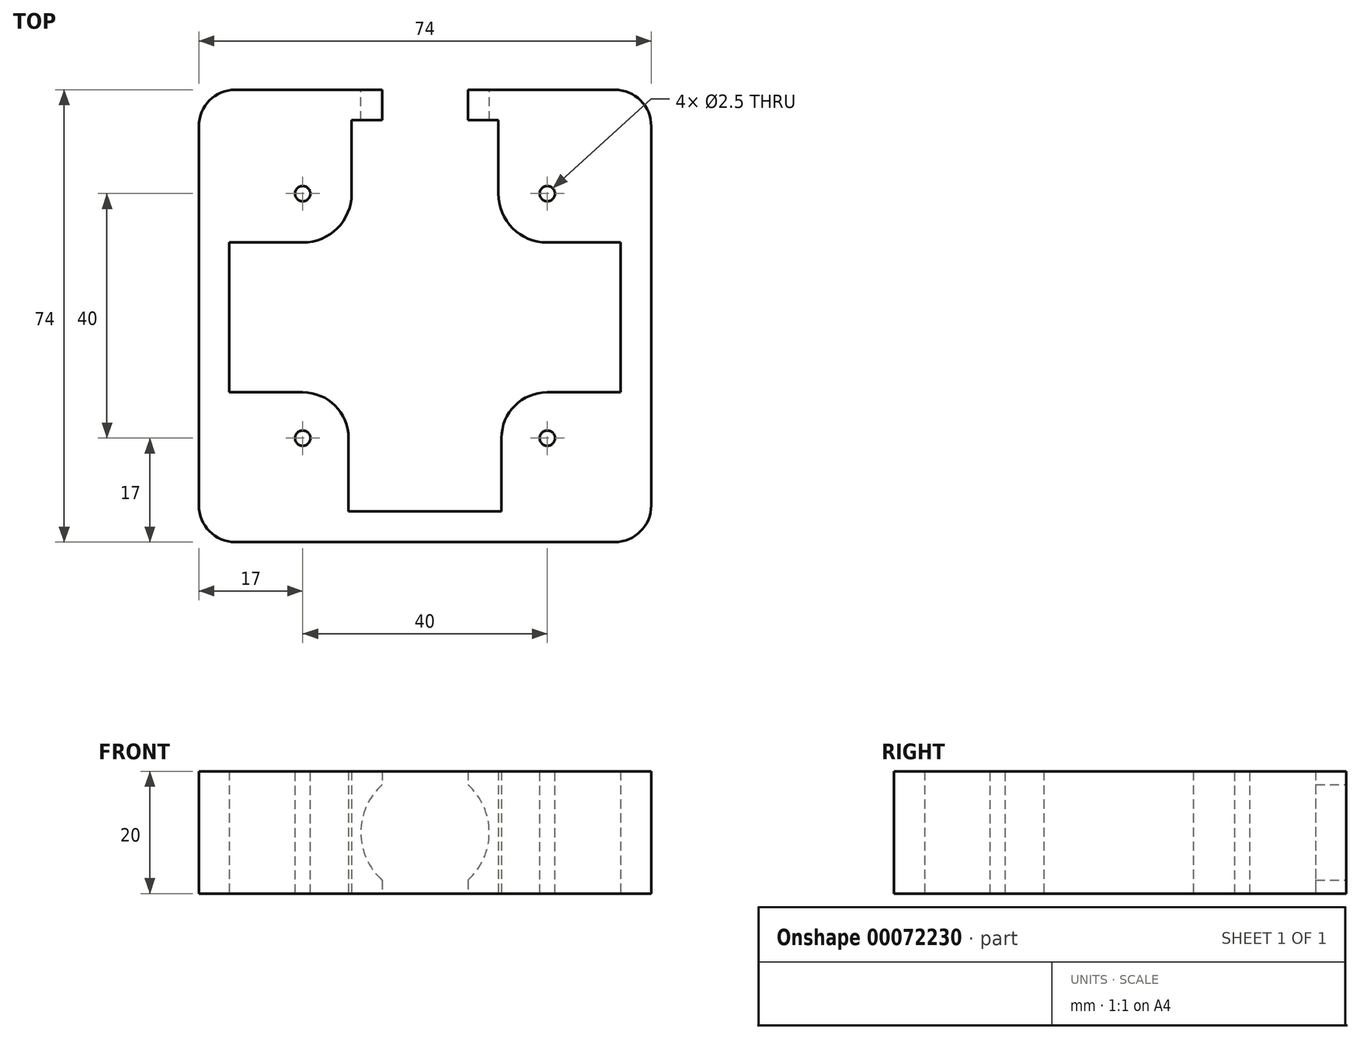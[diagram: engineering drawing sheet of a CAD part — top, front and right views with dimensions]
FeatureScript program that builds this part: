
annotation { "Feature Type Name" : "Feature", "Feature Type Description" : "" }
export const myFeature = defineFeature(function(context is Context, id is Id, definition is map)
    precondition{}
    {
        {
            var Q0;
            Q0=qCreatedBy(makeId("Top.planeOp"),FACE);
            var sketch = newSketch(context, id + "F0", { "sketchPlane" : qUnion([Q0])});
            skLineSegment(sketch, "E0.top", {"start": v(6, 74) * mm, "end": v(68, 74) * mm, "construction": true});
            skLineSegment(sketch, "E0.left", {"start": v(0, 6) * mm, "end": v(0, 68) * mm});
            skPoint(sketch, "E1.visualSharp", {"position": v(0, 74) * mm});
            skArc(sketch, "E1.filletArc", {"start": v(6, 74) * mm, "mid": v(1.76, 72.24) * mm, "end": v(0, 68) * mm});
            skPoint(sketch, "E2.visualSharp", {"position": v(0, 0) * mm});
            skArc(sketch, "E2.filletArc", {"start": v(0, 6) * mm, "mid": v(1.76, 1.76) * mm, "end": v(6, 0) * mm});
            skLineSegment(sketch, "E3", {"start": v(-6.9, 57) * mm, "end": v(92.75, 57) * mm, "construction": true});
            skLineSegment(sketch, "E4", {"start": v(17, 79.97) * mm, "end": v(17, -5.12) * mm, "construction": true});
            skLineSegment(sketch, "E5", {"start": v(-6.45, 17) * mm, "end": v(93.2, 17) * mm, "construction": true});
            skLineSegment(sketch, "E6", {"start": v(37, 80.67) * mm, "end": v(37, -9.85) * mm, "construction": true});
            skLineSegment(sketch, "E7", {"start": v(30, 74) * mm, "end": v(6, 74) * mm});
            skLineSegment(sketch, "E8", {"start": v(30, 69) * mm, "end": v(25, 69) * mm});
            skLineSegment(sketch, "E9", {"start": v(30, 69) * mm, "end": v(30, 74) * mm});
            skLineSegment(sketch, "E10", {"start": v(37, 0) * mm, "end": v(6, 0) * mm});
            skLineSegment(sketch, "E11.MirrorCS", {"start": v(44, 69) * mm, "end": v(49, 69) * mm});
            skArc(sketch, "E12.MirrorCS", {"start": v(68, 74) * mm, "mid": v(72.24, 72.24) * mm, "end": v(74, 68) * mm});
            skArc(sketch, "E13.MirrorCS", {"start": v(74, 6) * mm, "mid": v(72.24, 1.76) * mm, "end": v(68, 0) * mm});
            skLineSegment(sketch, "E14.MirrorCS", {"start": v(37, 0) * mm, "end": v(68, 0) * mm});
            skLineSegment(sketch, "E15.MirrorCS", {"start": v(44, 74) * mm, "end": v(68, 74) * mm});
            skLineSegment(sketch, "E16.MirrorCS", {"start": v(44, 69) * mm, "end": v(44, 74) * mm});
            skPoint(sketch, "E17.MirrorP", {"position": v(74, 74) * mm});
            skPoint(sketch, "E18.MirrorP", {"position": v(74, 0) * mm});
            skLineSegment(sketch, "E19.MirrorCS", {"start": v(74, 6) * mm, "end": v(74, 68) * mm});
            skLineSegment(sketch, "E20", {"start": v(24.5, 5) * mm, "end": v(49.5, 5) * mm});
            skArc(sketch, "E21", {"start": v(25, 57) * mm, "mid": v(22.66, 51.34) * mm, "end": v(17, 49) * mm});
            skArc(sketch, "E22", {"start": v(24.5, 17) * mm, "mid": v(22.3, 22.3) * mm, "end": v(17, 24.5) * mm});
            skLineSegment(sketch, "E23", {"start": v(17, 49) * mm, "end": v(5, 49) * mm});
            skLineSegment(sketch, "E24", {"start": v(5, 49) * mm, "end": v(5, 24.5) * mm});
            skLineSegment(sketch, "E25", {"start": v(5, 24.5) * mm, "end": v(17, 24.5) * mm});
            skLineSegment(sketch, "E26", {"start": v(25, 69) * mm, "end": v(25, 57) * mm});
            skLineSegment(sketch, "E27", {"start": v(24.5, 17) * mm, "end": v(24.5, 5) * mm});
            skLineSegment(sketch, "E28.MirrorCS", {"start": v(49, 69) * mm, "end": v(49, 57) * mm});
            skArc(sketch, "E29.MirrorCS", {"start": v(49, 57) * mm, "mid": v(51.34, 51.34) * mm, "end": v(57, 49) * mm});
            skLineSegment(sketch, "E30.MirrorCS", {"start": v(57, 49) * mm, "end": v(69, 49) * mm});
            skLineSegment(sketch, "E31.MirrorCS", {"start": v(69, 49) * mm, "end": v(69, 24.5) * mm});
            skLineSegment(sketch, "E32.MirrorCS", {"start": v(69, 24.5) * mm, "end": v(57, 24.5) * mm});
            skArc(sketch, "E33.MirrorCS", {"start": v(49.5, 17) * mm, "mid": v(51.7, 22.3) * mm, "end": v(57, 24.5) * mm});
            skLineSegment(sketch, "E34.MirrorCS", {"start": v(49.5, 17) * mm, "end": v(49.5, 5) * mm});
            skLineSegment(sketch, "E35.MirrorCS", {"start": v(49.5, 5) * mm, "end": v(24.5, 5) * mm});
            skSolve(sketch);
        }
        {
            var Q0;
            Q0 = qSketchRegion(id + "F0", true);
            extrude(context, id + "F1", {"entities" : qUnion([Q0]), "depth" : 20 * mm});
        }
        {
            var Q0;
            Q0=makeQuery(id+"F1.opExtrude","SWEPT_FACE",FACE,{"disambiguationData":[OSD([sQuery(id+"F0.wireOp",EDGE,"E15.MirrorCS")])]});
            var sketch = newSketch(context, id + "F2", { "sketchPlane" : qUnion([Q0])});
            skLineSegment(sketch, "E36", {"start": v(-68, 10) * mm, "end": v(-6, 10) * mm});
            skPoint(sketch, "E36.endSnap0", {"position": v(-68, 10) * mm});
            skCircle(sketch, "E37", {"center": v(-37, 10) * mm, "radius": 10.5 * mm});
            skSolve(sketch);
        }
        {
            var Q0;
            Q0 = qSketchRegion(id + "F2", true);
            extrude(context, id + "F3", {"entities" : qUnion([Q0]), "oppositeDirection" : true, "depth" : 25 * mm});
        }
        {
            var Q0;
            Q0=makeQuery(id+"F3.opExtrude","SWEPT_BODY",BODY,{"disambiguationData":[OSD([sQuery(id+"F2.wireOp",EDGE,"E37")])]});
            var Q1;
            Q1=makeQuery(id+"F1.opExtrude","SWEPT_BODY",BODY,{"disambiguationData":[OSD([sQuery(id+"F0.wireOp",EDGE,"E0.left"),sQuery(id+"F0.wireOp",EDGE,"E1.filletArc"),sQuery(id+"F0.wireOp",EDGE,"E2.filletArc"),sQuery(id+"F0.wireOp",EDGE,"Cqtl8sYd-x8eA-p0Ci-qh9f-KP0X5arBush6"),sQuery(id+"F0.wireOp",EDGE,"t0FDsQM7-GWqa-ov0J-h6zA-vYq5VfIPqZyT"),sQuery(id+"F0.wireOp",EDGE,"dZylRY6x-1Ij4-8kdU-HT9k-4JOX3FaVU0Y9"),sQuery(id+"F0.wireOp",EDGE,"j7dCo05Q-NK8S-PAB8-5yVi-hLkRdOoC1qtI"),sQuery(id+"F0.wireOp",EDGE,"QDbTKYnb-cyUq-QaIH-Lbgu-o2sDgkH0uhrb"),sQuery(id+"F0.wireOp",EDGE,"E7"),sQuery(id+"F0.wireOp",EDGE,"E8"),sQuery(id+"F0.wireOp",EDGE,"iqIQcJiS-4jgR-Reb2-r4IF-rO4RF3F6gWLn"),sQuery(id+"F0.wireOp",EDGE,"E9"),sQuery(id+"F0.wireOp",EDGE,"E10"),sQuery(id+"F0.wireOp",EDGE,"zJ4gfM54-7Wjp-qNnH-eqyB-9P3vSi8HfcG8"),sQuery(id+"F0.wireOp",EDGE,"E11.MirrorCS"),sQuery(id+"F0.wireOp",EDGE,"E12.MirrorCS"),sQuery(id+"F0.wireOp",EDGE,"abba0434-76aa-401e-ba99-632714cfb67c3.MirrorCS"),sQuery(id+"F0.wireOp",EDGE,"E13.MirrorCS"),sQuery(id+"F0.wireOp",EDGE,"abba0434-76aa-401e-ba99-632714cfb67c6.MirrorCS"),sQuery(id+"F0.wireOp",EDGE,"E14.MirrorCS"),sQuery(id+"F0.wireOp",EDGE,"E15.MirrorCS"),sQuery(id+"F0.wireOp",EDGE,"E16.MirrorCS"),sQuery(id+"F0.wireOp",EDGE,"abba0434-76aa-401e-ba99-632714cfb67c10.MirrorCS"),sQuery(id+"F0.wireOp",EDGE,"abba0434-76aa-401e-ba99-632714cfb67c12.MirrorCS"),sQuery(id+"F0.wireOp",EDGE,"abba0434-76aa-401e-ba99-632714cfb67c14.MirrorCS"),sQuery(id+"F0.wireOp",EDGE,"abba0434-76aa-401e-ba99-632714cfb67c15.MirrorCS"),sQuery(id+"F0.wireOp",EDGE,"abba0434-76aa-401e-ba99-632714cfb67c16.MirrorCS"),sQuery(id+"F0.wireOp",EDGE,"E19.MirrorCS")])]});
            booleanBodies(context, id + "F4", {"operationType" : BooleanOperationType.SUBTRACTION, "tools" : qUnion([Q0]), "targets" : qUnion([Q1])});
        }
        {
            var Q0;
            Q0=makeQuery(id+"F1.opExtrude","CAP_FACE",FACE,{"disambiguationData":[OSD([sQuery(id+"F0.wireOp",EDGE,"E0.left"),sQuery(id+"F0.wireOp",EDGE,"E1.filletArc"),sQuery(id+"F0.wireOp",EDGE,"E2.filletArc"),sQuery(id+"F0.wireOp",EDGE,"E7"),sQuery(id+"F0.wireOp",EDGE,"E8"),sQuery(id+"F0.wireOp",EDGE,"E9"),sQuery(id+"F0.wireOp",EDGE,"E10"),sQuery(id+"F0.wireOp",EDGE,"E11.MirrorCS"),sQuery(id+"F0.wireOp",EDGE,"E12.MirrorCS"),sQuery(id+"F0.wireOp",EDGE,"E13.MirrorCS"),sQuery(id+"F0.wireOp",EDGE,"E14.MirrorCS"),sQuery(id+"F0.wireOp",EDGE,"E15.MirrorCS"),sQuery(id+"F0.wireOp",EDGE,"E16.MirrorCS"),sQuery(id+"F0.wireOp",EDGE,"E19.MirrorCS"),sQuery(id+"F0.wireOp",EDGE,"E21"),sQuery(id+"F0.wireOp",EDGE,"E22"),sQuery(id+"F0.wireOp",EDGE,"E23"),sQuery(id+"F0.wireOp",EDGE,"E24"),sQuery(id+"F0.wireOp",EDGE,"E25"),sQuery(id+"F0.wireOp",EDGE,"E26"),sQuery(id+"F0.wireOp",EDGE,"E27"),sQuery(id+"F0.wireOp",EDGE,"E28.MirrorCS"),sQuery(id+"F0.wireOp",EDGE,"E29.MirrorCS"),sQuery(id+"F0.wireOp",EDGE,"E30.MirrorCS"),sQuery(id+"F0.wireOp",EDGE,"E31.MirrorCS"),sQuery(id+"F0.wireOp",EDGE,"E32.MirrorCS"),sQuery(id+"F0.wireOp",EDGE,"E33.MirrorCS"),sQuery(id+"F0.wireOp",EDGE,"E34.MirrorCS"),sQuery(id+"F0.wireOp",EDGE,"E35.MirrorCS")])],"isStart":false});
            var sketch = newSketch(context, id + "F5", { "sketchPlane" : qUnion([Q0])});
            skPoint(sketch, "E38", {"position": v(57, 57) * mm});
            skPoint(sketch, "E39", {"position": v(17, 57) * mm});
            skPoint(sketch, "E40", {"position": v(17, 17) * mm});
            skPoint(sketch, "E41", {"position": v(57, 17) * mm});
            skSolve(sketch);
        }
        {
            var Q0;
            Q0=sQuery(id+"F5.wireOp",VERTEX,"E39");
            var Q1;
            Q1=sQuery(id+"F5.wireOp",VERTEX,"E38");
            var Q2;
            Q2=sQuery(id+"F5.wireOp",VERTEX,"E41");
            var Q3;
            Q3=sQuery(id+"F5.wireOp",VERTEX,"E40");
            var Q4;
            Q4=makeQuery(id+"F1.opExtrude","SWEPT_BODY",BODY,{"disambiguationData":[OSD([sQuery(id+"F0.wireOp",EDGE,"E0.left"),sQuery(id+"F0.wireOp",EDGE,"E1.filletArc"),sQuery(id+"F0.wireOp",EDGE,"E2.filletArc"),sQuery(id+"F0.wireOp",EDGE,"E7"),sQuery(id+"F0.wireOp",EDGE,"E8"),sQuery(id+"F0.wireOp",EDGE,"E9"),sQuery(id+"F0.wireOp",EDGE,"E10"),sQuery(id+"F0.wireOp",EDGE,"E11.MirrorCS"),sQuery(id+"F0.wireOp",EDGE,"E12.MirrorCS"),sQuery(id+"F0.wireOp",EDGE,"E13.MirrorCS"),sQuery(id+"F0.wireOp",EDGE,"E14.MirrorCS"),sQuery(id+"F0.wireOp",EDGE,"E15.MirrorCS"),sQuery(id+"F0.wireOp",EDGE,"E16.MirrorCS"),sQuery(id+"F0.wireOp",EDGE,"E19.MirrorCS"),sQuery(id+"F0.wireOp",EDGE,"E21"),sQuery(id+"F0.wireOp",EDGE,"E22"),sQuery(id+"F0.wireOp",EDGE,"E23"),sQuery(id+"F0.wireOp",EDGE,"E24"),sQuery(id+"F0.wireOp",EDGE,"E25"),sQuery(id+"F0.wireOp",EDGE,"E26"),sQuery(id+"F0.wireOp",EDGE,"E27"),sQuery(id+"F0.wireOp",EDGE,"E28.MirrorCS"),sQuery(id+"F0.wireOp",EDGE,"E29.MirrorCS"),sQuery(id+"F0.wireOp",EDGE,"E30.MirrorCS"),sQuery(id+"F0.wireOp",EDGE,"E31.MirrorCS"),sQuery(id+"F0.wireOp",EDGE,"E32.MirrorCS"),sQuery(id+"F0.wireOp",EDGE,"E33.MirrorCS"),sQuery(id+"F0.wireOp",EDGE,"E34.MirrorCS"),sQuery(id+"F0.wireOp",EDGE,"E35.MirrorCS")])]});
            hole(context, id + "F6", {"style" : HoleStyle.SIMPLE, "endStyle" : HoleEndStyle.THROUGH, "holeDiameter" : 2.5 * mm, "locations" : qUnion([Q0, Q1, Q2, Q3]), "scope" : qUnion([Q4]), "isTappedThrough" : true});
        }
    });
